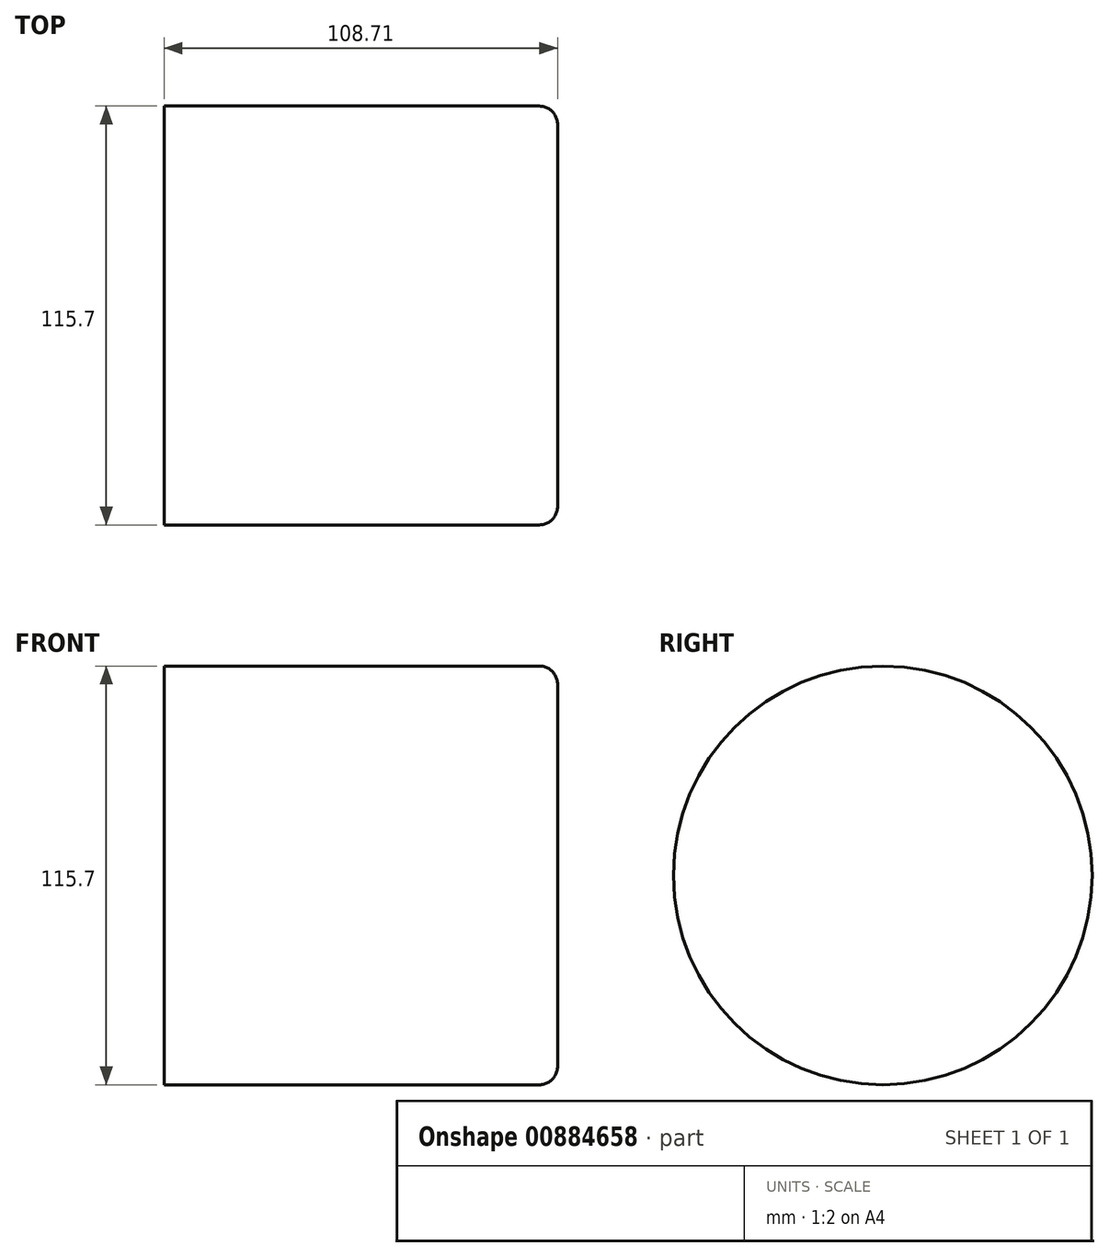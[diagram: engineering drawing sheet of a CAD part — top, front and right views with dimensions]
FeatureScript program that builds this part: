
annotation { "Feature Type Name" : "Feature", "Feature Type Description" : "" }
export const myFeature = defineFeature(function(context is Context, id is Id, definition is map)
    precondition{}
    {
        {
            var Q0;
            Q0=qCreatedBy(makeId("Right.planeOp"),FACE);
            var sketch = newSketch(context, id + "F0", { "sketchPlane" : qUnion([Q0])});
            skCircle(sketch, "E0", {"center": v(0, 0) * mm, "radius": 57.85 * mm});
            skSolve(sketch);
        }
        {
            var Q0;
            Q0=makeQuery(id+"F0.imprint","IMPRINT",FACE,{"disambiguationData":[TD([[makeQuery(id+"F0.imprint","IMPRINT",EDGE,{"derivedFrom":sQuery(id+"F0.wireOp",EDGE,"E0")}),1.0]])]});
            extrude(context, id + "F1", {"entities" : qUnion([Q0]), "depth" : 108.7 * mm, "offsetDistance" : 25.4 * mm});
        }
        {
            var Q0;
            Q0=makeQuery(id+"F1.opExtrude","CAP_EDGE",EDGE,{"disambiguationData":[OSD([sQuery(id+"F0.wireOp",EDGE,"E0")])],"isStart":false});
            fillet(context, id + "F2", {"entities" : qUnion([Q0]), "radius" : 5.08 * mm, "tangentPropagation" : true, "allowEdgeOverflow" : false});
        }
    });
